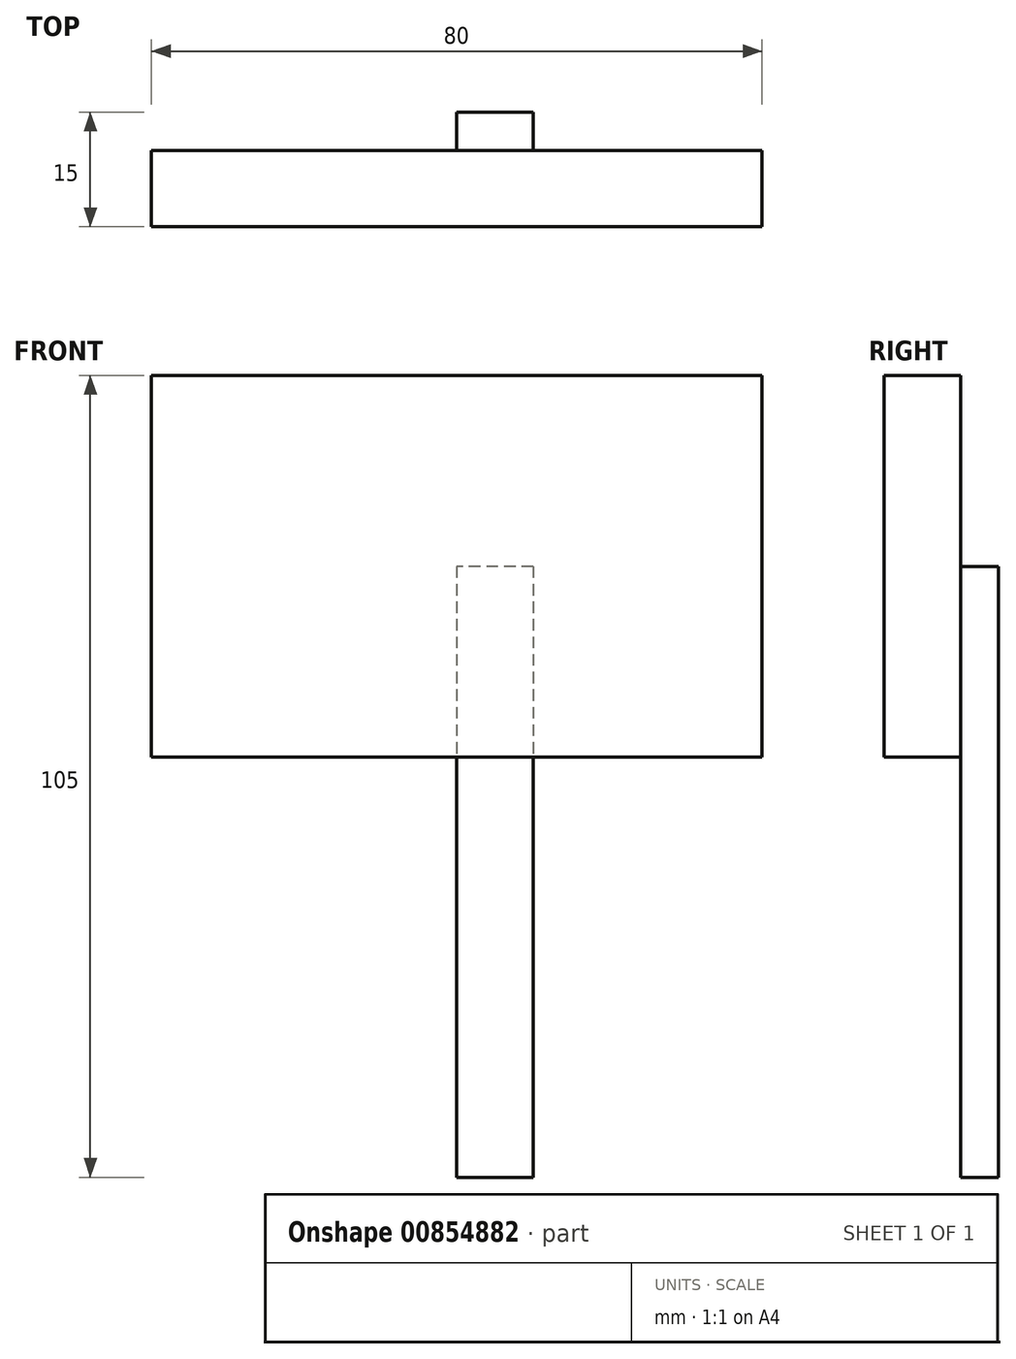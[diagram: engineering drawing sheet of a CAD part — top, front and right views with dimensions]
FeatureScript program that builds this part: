
annotation { "Feature Type Name" : "Feature", "Feature Type Description" : "" }
export const myFeature = defineFeature(function(context is Context, id is Id, definition is map)
    precondition{}
    {
        {
            var Q0;
            Q0=qCreatedBy(makeId("Front.planeOp"),FACE);
            var sketch = newSketch(context, id + "F0", { "sketchPlane" : qUnion([Q0])});
            skLineSegment(sketch, "E0.bottom", {"start": v(40, 25) * mm, "end": v(-40, 25) * mm});
            skLineSegment(sketch, "E0.top", {"start": v(40, -25) * mm, "end": v(-40, -25) * mm});
            skLineSegment(sketch, "E0.left", {"start": v(40, 25) * mm, "end": v(40, -25) * mm});
            skLineSegment(sketch, "E0.right", {"start": v(-40, 25) * mm, "end": v(-40, -25) * mm});
            skPoint(sketch, "E0.middle", {"position": v(0, 0) * mm});
            skSolve(sketch);
        }
        {
            var Q0;
            Q0 = qSketchRegion(id + "F0", true);
            extrude(context, id + "F1", {"entities" : qUnion([Q0]), "depth" : 10 * mm, "offsetDistance" : 25.4 * mm});
        }
        {
            var Q0;
            Q0=qCreatedBy(makeId("Right.planeOp"),FACE);
            var sketch = newSketch(context, id + "F2", { "sketchPlane" : qUnion([Q0])});
            skLineSegment(sketch, "E1.bottom", {"start": v(0, 0) * mm, "end": v(5, 0) * mm});
            skLineSegment(sketch, "E1.top", {"start": v(0, -80) * mm, "end": v(5, -80) * mm});
            skLineSegment(sketch, "E1.left", {"start": v(0, 0) * mm, "end": v(0, -80) * mm});
            skLineSegment(sketch, "E1.right", {"start": v(5, 0) * mm, "end": v(5, -80) * mm});
            skSolve(sketch);
        }
        {
            var Q0;
            Q0 = qSketchRegion(id + "F2", true);
            extrude(context, id + "F3", {"entities" : qUnion([Q0]), "operationType" : NewBodyOperationType.ADD, "depth" : 10 * mm, "offsetDistance" : 25.4 * mm});
        }
    });
